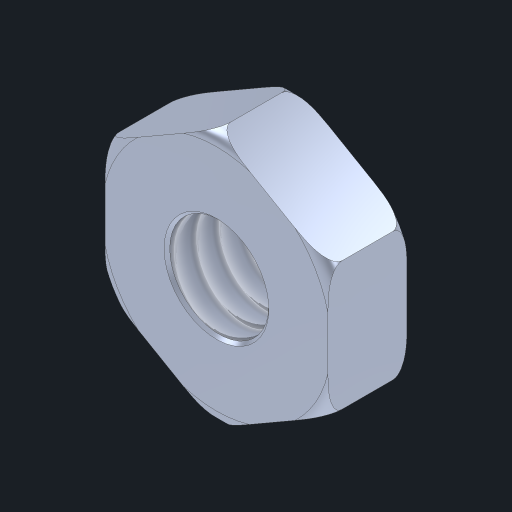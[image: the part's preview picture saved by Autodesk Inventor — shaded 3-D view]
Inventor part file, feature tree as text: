
AUTODESK INVENTOR PART (.ipt)
format: ipt  version: 2023 (Build 270158030, 158C)  size: 202,752 bytes
history: native  units: in
note: dims shown in document units (in); Inventor stores cm internally (conversion verified against a paired STEP export)
features: thread x1
ambient origin geometry x8: Origin, YZ Plane, XZ Plane, XY Plane, X Axis, Y Axis, Z Axis, Center Point
bodies: Solid2 (feature_tree), Solid1 (feature_tree)
feature tree (1):
  thread  "Thread1"  [1 undecoded]
note: 1 required parameter value undecoded (feature->parameter linkage not recoverable at this tier; creation-order binding heuristic only, values carry confidence <= 0.55)
